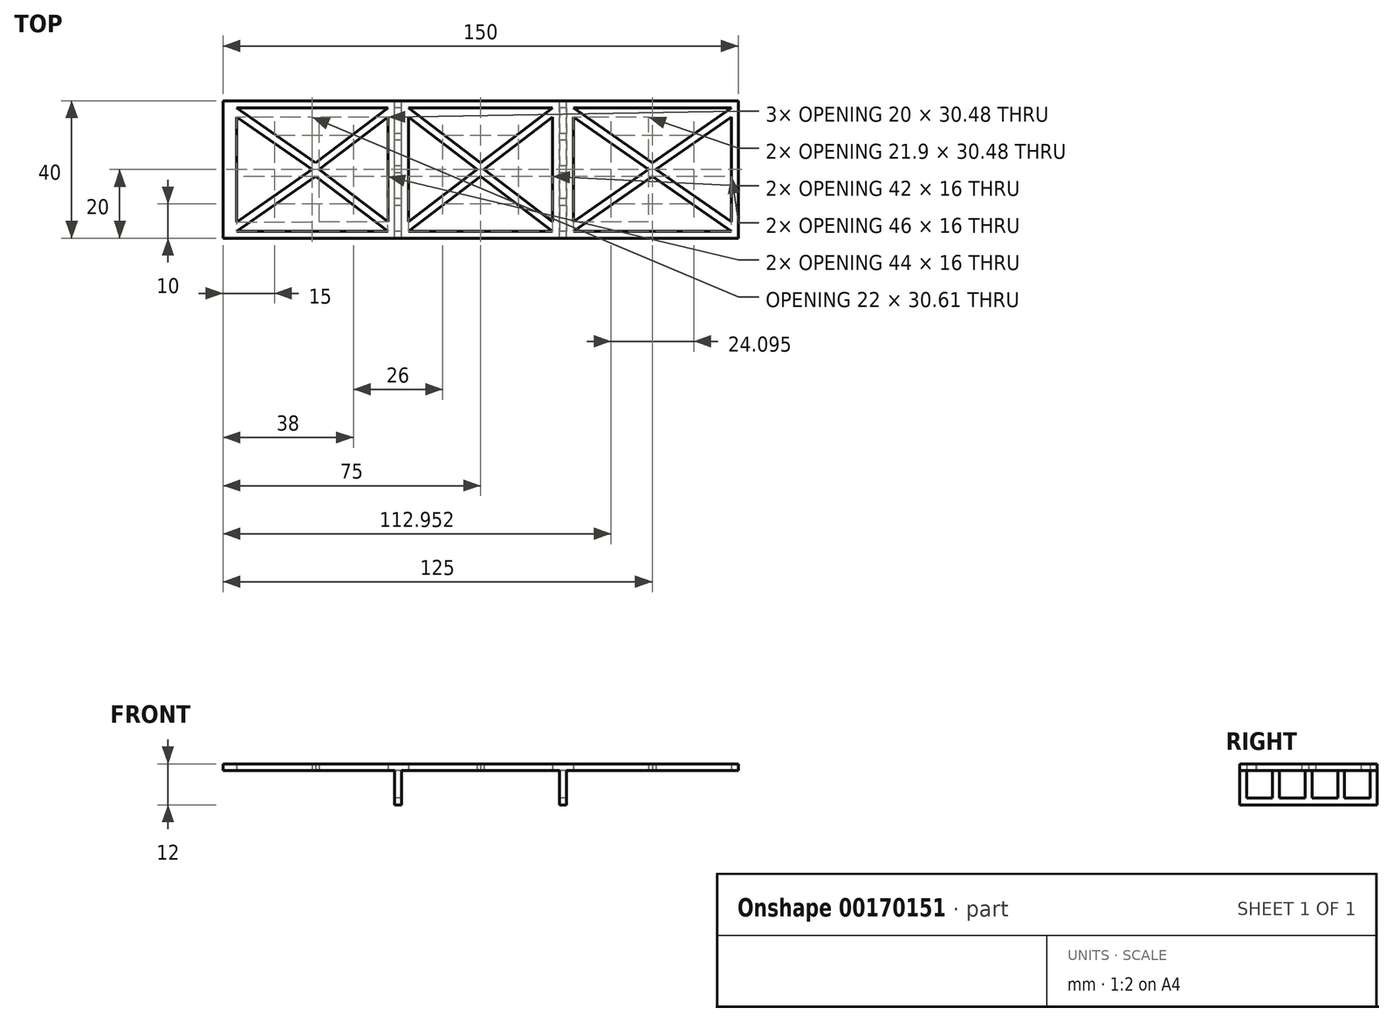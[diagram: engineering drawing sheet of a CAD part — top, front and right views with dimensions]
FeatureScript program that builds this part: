
annotation { "Feature Type Name" : "Feature", "Feature Type Description" : "" }
export const myFeature = defineFeature(function(context is Context, id is Id, definition is map)
    precondition{}
    {
        {
            var Q0;
            Q0=qCreatedBy(makeId("Front.planeOp"),FACE);
            var sketch = newSketch(context, id + "F0", { "sketchPlane" : qUnion([Q0])});
            skLineSegment(sketch, "E0", {"start": v(-75, 0) * mm, "end": v(75, 0) * mm});
            skLineSegment(sketch, "E1", {"start": v(-75, 0) * mm, "end": v(-75, -2) * mm});
            skLineSegment(sketch, "E2", {"start": v(-75, -2) * mm, "end": v(-25, -2) * mm});
            skLineSegment(sketch, "E3", {"start": v(-25, -2) * mm, "end": v(-25, -12) * mm});
            skLineSegment(sketch, "E4", {"start": v(-25, -12) * mm, "end": v(-23, -12) * mm});
            skLineSegment(sketch, "E5", {"start": v(-23, -12) * mm, "end": v(-23, -2) * mm});
            skLineSegment(sketch, "E6", {"start": v(-23, -2) * mm, "end": v(23, -2) * mm});
            skLineSegment(sketch, "E7", {"start": v(23, -2) * mm, "end": v(23, -12) * mm});
            skLineSegment(sketch, "E8", {"start": v(23, -12) * mm, "end": v(25, -12) * mm});
            skLineSegment(sketch, "E9", {"start": v(25, -12) * mm, "end": v(25, -2) * mm});
            skLineSegment(sketch, "E10", {"start": v(25, -2) * mm, "end": v(75, -2) * mm});
            skLineSegment(sketch, "E11", {"start": v(75, -2) * mm, "end": v(75, 0) * mm});
            skSolve(sketch);
        }
        {
            var Q0;
            Q0 = qSketchRegion(id + "F0", true);
            extrude(context, id + "F1", {"entities" : qUnion([Q0]), "endBound" : BoundingType.SYMMETRIC, "depth" : 40 * mm});
        }
        {
            var Q0;
            Q0=makeQuery(id+"F1.opExtrude","SWEPT_FACE",FACE,{"disambiguationData":[OSD([sQuery(id+"F0.wireOp",EDGE,"E2")])]});
            var sketch = newSketch(context, id + "F2", { "sketchPlane" : qUnion([Q0])});
            skLineSegment(sketch, "E12", {"start": v(-71, 18) * mm, "end": v(-27, 18) * mm});
            skLineSegment(sketch, "E13", {"start": v(-27, 18) * mm, "end": v(-48, 2) * mm});
            skLineSegment(sketch, "E14", {"start": v(-48, 2) * mm, "end": v(-71, 18) * mm});
            skLineSegment(sketch, "E15", {"start": v(-75, 0) * mm, "end": v(74.76, 0) * mm, "construction": true});
            skLineSegment(sketch, "E16", {"start": v(-21, 18) * mm, "end": v(21, 18) * mm});
            skLineSegment(sketch, "E17", {"start": v(21, 18) * mm, "end": v(0, 2) * mm});
            skLineSegment(sketch, "E18", {"start": v(0, 2) * mm, "end": v(-21, 18) * mm});
            skLineSegment(sketch, "E19", {"start": v(27, 18) * mm, "end": v(73, 18) * mm});
            skLineSegment(sketch, "E20", {"start": v(73, 18) * mm, "end": v(50, 2) * mm});
            skPoint(sketch, "E20.endSnap0", {"position": v(50, 18) * mm});
            skLineSegment(sketch, "E21", {"start": v(50, 2) * mm, "end": v(27, 18) * mm});
            skLineSegment(sketch, "E22.MirrorCS", {"start": v(-48, -2) * mm, "end": v(-71, -18) * mm});
            skLineSegment(sketch, "E23.MirrorCS", {"start": v(-71, -18) * mm, "end": v(-27, -18) * mm});
            skLineSegment(sketch, "E24.MirrorCS", {"start": v(-27, -18) * mm, "end": v(-48, -2) * mm});
            skLineSegment(sketch, "E25.MirrorCS", {"start": v(0, -2) * mm, "end": v(-21, -18) * mm});
            skLineSegment(sketch, "E26.MirrorCS", {"start": v(-21, -18) * mm, "end": v(21, -18) * mm});
            skLineSegment(sketch, "E27.MirrorCS", {"start": v(21, -18) * mm, "end": v(0, -2) * mm});
            skLineSegment(sketch, "E28.MirrorCS", {"start": v(50, -2) * mm, "end": v(27, -18) * mm});
            skLineSegment(sketch, "E29.MirrorCS", {"start": v(27, -18) * mm, "end": v(73, -18) * mm});
            skLineSegment(sketch, "E30.MirrorCS", {"start": v(73, -18) * mm, "end": v(50, -2) * mm});
            skLineSegment(sketch, "E31", {"start": v(-71, 15.3) * mm, "end": v(-49, 0) * mm});
            skLineSegment(sketch, "E32", {"start": v(-49, 0) * mm, "end": v(-71, -15.3) * mm});
            skLineSegment(sketch, "E33", {"start": v(-71, -15.3) * mm, "end": v(-71, 15.3) * mm});
            skLineSegment(sketch, "E34", {"start": v(-27, 15.24) * mm, "end": v(-47, 0) * mm});
            skLineSegment(sketch, "E35", {"start": v(-47, 0) * mm, "end": v(-27, -15.24) * mm});
            skLineSegment(sketch, "E36", {"start": v(-27, -15.24) * mm, "end": v(-27, 15.24) * mm});
            skLineSegment(sketch, "E37", {"start": v(-21, 15.24) * mm, "end": v(-1, 0) * mm});
            skLineSegment(sketch, "E38", {"start": v(-1, 0) * mm, "end": v(-21, -15.24) * mm});
            skLineSegment(sketch, "E39", {"start": v(-21, -15.24) * mm, "end": v(-21, 15.24) * mm});
            skLineSegment(sketch, "E40", {"start": v(21, 15.24) * mm, "end": v(1, 0) * mm});
            skLineSegment(sketch, "E41", {"start": v(1, 0) * mm, "end": v(21, -15.24) * mm});
            skLineSegment(sketch, "E42", {"start": v(21, -15.24) * mm, "end": v(21, 15.24) * mm});
            skLineSegment(sketch, "E43", {"start": v(27, 15.24) * mm, "end": v(27, -15.24) * mm});
            skLineSegment(sketch, "E44", {"start": v(27, -15.24) * mm, "end": v(48.9, 0) * mm});
            skLineSegment(sketch, "E45", {"start": v(48.9, 0) * mm, "end": v(27, 15.24) * mm});
            skLineSegment(sketch, "E46", {"start": v(73, 15.24) * mm, "end": v(51.1, 0) * mm});
            skLineSegment(sketch, "E47", {"start": v(51.1, 0) * mm, "end": v(73, -15.24) * mm});
            skLineSegment(sketch, "E48", {"start": v(73, -15.24) * mm, "end": v(73, 15.24) * mm});
            skSolve(sketch);
        }
        {
            var Q0;
            Q0 = qSketchRegion(id + "F2", true);
            var Q1;
            Q1=makeQuery(id+"F1.opExtrude","SWEPT_FACE",FACE,{"disambiguationData":[OSD([sQuery(id+"F0.wireOp",EDGE,"E0")])]});
            extrude(context, id + "F3", {"entities" : qUnion([Q0]), "operationType" : NewBodyOperationType.REMOVE, "endBound" : BoundingType.UP_TO_SURFACE, "oppositeDirection" : true, "endBoundEntityFace" : qUnion([Q1]), "depth" : 25 * mm});
        }
        {
            var Q0;
            Q0=makeQuery(id+"F1.opExtrude","SWEPT_FACE",FACE,{"disambiguationData":[OSD([sQuery(id+"F0.wireOp",EDGE,"E7")])]});
            var sketch = newSketch(context, id + "F4", { "sketchPlane" : qUnion([Q0])});
            skLineSegment(sketch, "E49.bottom", {"start": v(18, -10) * mm, "end": v(10.5, -10) * mm});
            skLineSegment(sketch, "E49.top", {"start": v(18, -2) * mm, "end": v(10.5, -2) * mm});
            skLineSegment(sketch, "E49.left", {"start": v(18, -10) * mm, "end": v(18, -2) * mm});
            skLineSegment(sketch, "E49.right", {"start": v(10.5, -10) * mm, "end": v(10.5, -2) * mm});
            skLineSegment(sketch, "E50.bottom", {"start": v(8.5, -10) * mm, "end": v(1, -10) * mm});
            skLineSegment(sketch, "E50.top", {"start": v(8.5, -2) * mm, "end": v(1, -2) * mm});
            skLineSegment(sketch, "E50.left", {"start": v(8.5, -10) * mm, "end": v(8.5, -2) * mm});
            skLineSegment(sketch, "E50.right", {"start": v(1, -10) * mm, "end": v(1, -2) * mm});
            skLineSegment(sketch, "E51.bottom", {"start": v(-1, -10) * mm, "end": v(-8.5, -10) * mm});
            skLineSegment(sketch, "E51.top", {"start": v(-1, -2) * mm, "end": v(-8.5, -2) * mm});
            skLineSegment(sketch, "E51.left", {"start": v(-1, -10) * mm, "end": v(-1, -2) * mm});
            skLineSegment(sketch, "E51.right", {"start": v(-8.5, -10) * mm, "end": v(-8.5, -2) * mm});
            skLineSegment(sketch, "E52.bottom", {"start": v(-10.5, -10) * mm, "end": v(-18, -10) * mm});
            skLineSegment(sketch, "E52.top", {"start": v(-10.5, -2) * mm, "end": v(-18, -2) * mm});
            skLineSegment(sketch, "E52.left", {"start": v(-10.5, -10) * mm, "end": v(-10.5, -2) * mm});
            skLineSegment(sketch, "E52.right", {"start": v(-18, -10) * mm, "end": v(-18, -2) * mm});
            skSolve(sketch);
        }
        {
            var Q0;
            Q0 = qSketchRegion(id + "F4", true);
            var Q1;
            Q1=makeQuery(id+"F1.opExtrude","SWEPT_FACE",FACE,{"disambiguationData":[OSD([sQuery(id+"F0.wireOp",EDGE,"E9")])]});
            var Q2;
            Q2=makeQuery(id+"F1.opExtrude","SWEPT_FACE",FACE,{"disambiguationData":[OSD([sQuery(id+"F0.wireOp",EDGE,"E3")])]});
            extrude(context, id + "F5", {"entities" : qUnion([Q0]), "operationType" : NewBodyOperationType.REMOVE, "endBound" : BoundingType.UP_TO_SURFACE, "oppositeDirection" : true, "endBoundEntityFace" : qUnion([Q1]), "depth" : 25 * mm, "hasSecondDirection" : true, "secondDirectionBound" : SecondDirectionBoundingType.UP_TO_SURFACE, "secondDirectionOppositeDirection" : false, "secondDirectionBoundEntityFace" : qUnion([Q2]), "secondDirectionDepth" : 25 * mm});
        }
    });
